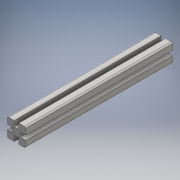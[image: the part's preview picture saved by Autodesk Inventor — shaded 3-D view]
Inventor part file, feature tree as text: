
AUTODESK INVENTOR PART (.ipt)
format: ipt  version: 2016 (Build 200138000, 138)  size: 120,320 bytes
history: native  units: mm
features: extrude x1, sketch x1
ambient origin geometry x8: Origin, YZ Plane, XZ Plane, XY Plane, X Axis, Y Axis, Z Axis, Center Point
bodies: Solid1 (feature_tree)
feature tree (2):
  extrude  "Extrusion1"  [1 undecoded]
  sketch  "Sketch1"  dims[d0=320.0mm d1=0.0mm]
note: 1 required parameter value undecoded (feature->parameter linkage not recoverable at this tier; creation-order binding heuristic only, values carry confidence <= 0.55)
